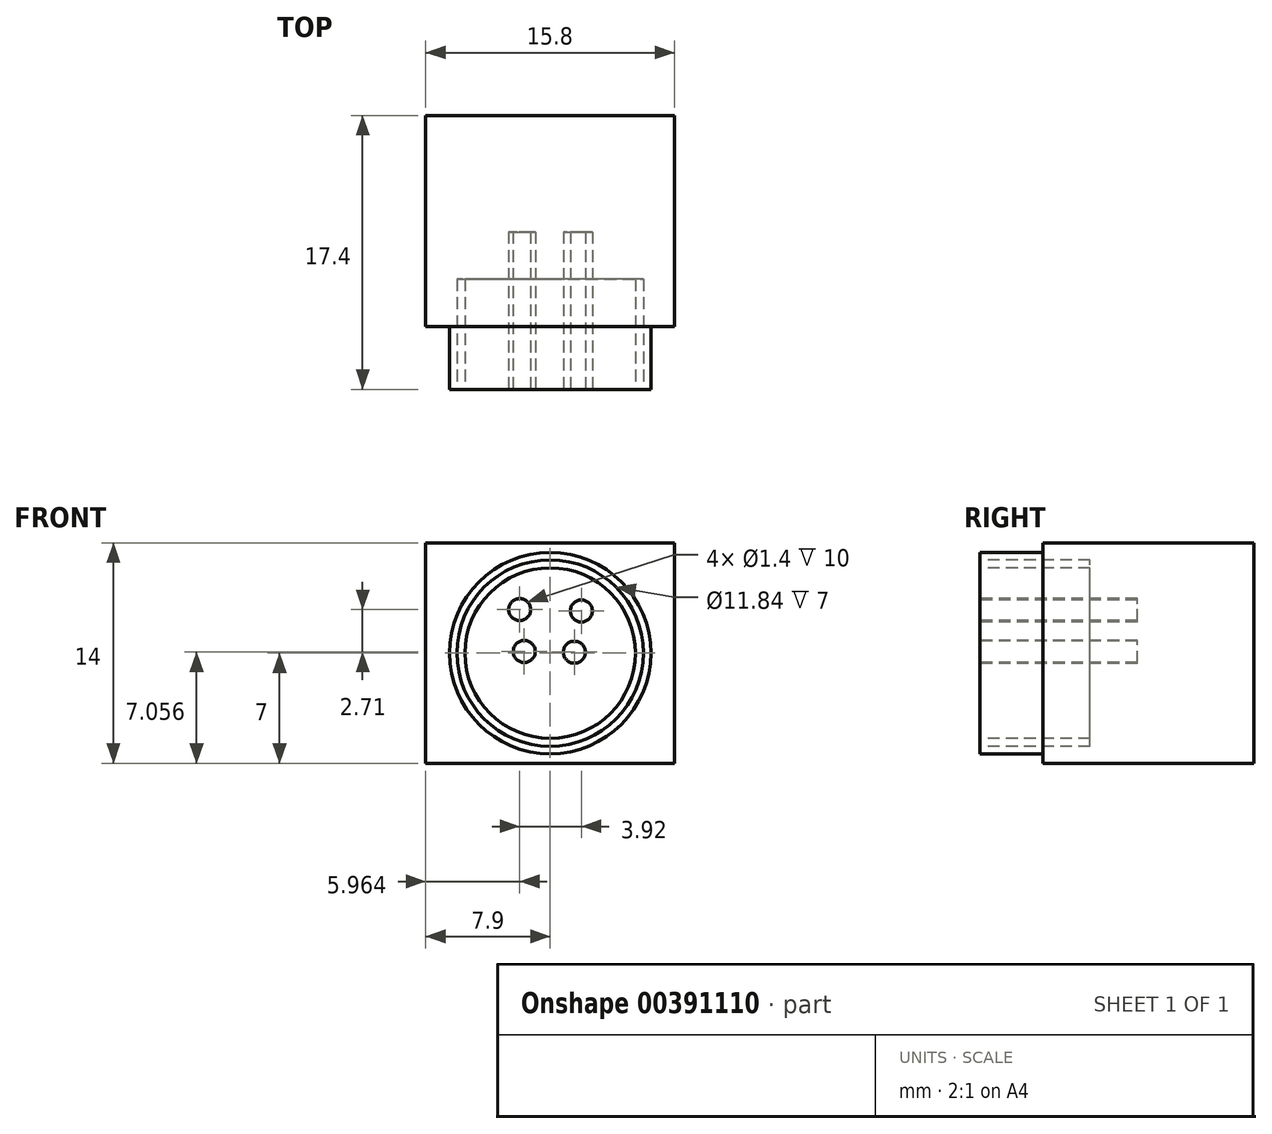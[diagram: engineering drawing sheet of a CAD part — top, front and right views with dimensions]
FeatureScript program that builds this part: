
annotation { "Feature Type Name" : "Feature", "Feature Type Description" : "" }
export const myFeature = defineFeature(function(context is Context, id is Id, definition is map)
    precondition{}
    {
        {
            var Q0;
            Q0=qCreatedBy(makeId("Front.planeOp"),FACE);
            var sketch = newSketch(context, id + "F0", { "sketchPlane" : qUnion([Q0])});
            skLineSegment(sketch, "E0.bottom", {"start": v(0, 0) * mm, "end": v(15.8, 0) * mm});
            skLineSegment(sketch, "E0.top", {"start": v(0, 14) * mm, "end": v(15.8, 14) * mm});
            skLineSegment(sketch, "E0.left", {"start": v(0, 0) * mm, "end": v(0, 14) * mm});
            skLineSegment(sketch, "E0.right", {"start": v(15.8, 0) * mm, "end": v(15.8, 14) * mm});
            skSolve(sketch);
        }
        {
            var Q0;
            Q0=qSketchRegion(id+"F0",true);
            extrude(context, id + "F1", {"entities" : qUnion([Q0]), "depth" : 13.4 * mm});
        }
        {
            var Q0;
            Q0=makeQuery(id+"F1.opExtrude","CAP_FACE",FACE,{"disambiguationData":[OSD([sQuery(id+"F0.wireOp",EDGE,"E0.bottom"),sQuery(id+"F0.wireOp",EDGE,"E0.top"),sQuery(id+"F0.wireOp",EDGE,"E0.left"),sQuery(id+"F0.wireOp",EDGE,"E0.right")])],"isStart":false});
            var sketch = newSketch(context, id + "F2", { "sketchPlane" : qUnion([Q0])});
            skCircle(sketch, "E1", {"center": v(7.9, 7) * mm, "radius": 6.4 * mm});
            skPoint(sketch, "E1.centerSnap0", {"position": v(15.8, 7) * mm});
            skPoint(sketch, "E1.centerSnap1", {"position": v(7.9, 14) * mm});
            skSolve(sketch);
        }
        {
            var Q0;
            Q0=qSketchRegion(id+"F2",true);
            extrude(context, id + "F3", {"entities" : qUnion([Q0]), "operationType" : NewBodyOperationType.ADD, "depth" : 4 * mm});
        }
        {
            var Q0;
            Q0=makeQuery(id+"F3.opExtrude","CAP_FACE",FACE,{"disambiguationData":[OSD([sQuery(id+"F2.wireOp",EDGE,"E1")])],"isStart":false});
            var sketch = newSketch(context, id + "F4", { "sketchPlane" : qUnion([Q0])});
            skCircle(sketch, "E2", {"center": v(7.9, 7) * mm, "radius": 5.92 * mm});
            skCircle(sketch, "E3", {"center": v(7.9, 7) * mm, "radius": 5.41 * mm});
            skSolve(sketch);
        }
        {
            var Q0;
            Q0=qSketchRegion(id+"F4",true);
            extrude(context, id + "F5", {"entities" : qUnion([Q0]), "operationType" : NewBodyOperationType.REMOVE, "oppositeDirection" : true, "depth" : 7 * mm});
        }
        {
            var Q0;
            Q0=makeQuery(id+"F5.boolean.opBoolean","SPLIT",FACE,{"disambiguationData":[TD([makeQuery(id+"F5.opExtrude","SWEPT_FACE",FACE,{"disambiguationData":[OSD([sQuery(id+"F4.wireOp",EDGE,"E3")])]})])],"derivedFrom":makeQuery(id+"F3.opExtrude","CAP_FACE",FACE,{"disambiguationData":[OSD([sQuery(id+"F2.wireOp",EDGE,"E1")])],"isStart":false})});
            var sketch = newSketch(context, id + "F6", { "sketchPlane" : qUnion([Q0])});
            skCircle(sketch, "E4", {"center": v(5.96, 9.77) * mm, "radius": 0.7 * mm});
            skCircle(sketch, "E5", {"center": v(9.88, 9.68) * mm, "radius": 0.7 * mm});
            skCircle(sketch, "E6", {"center": v(6.26, 7.1) * mm, "radius": 0.7 * mm});
            skCircle(sketch, "E7", {"center": v(9.44, 7.06) * mm, "radius": 0.7 * mm});
            skSolve(sketch);
        }
        {
            var Q0;
            Q0=qSketchRegion(id+"F6",true);
            extrude(context, id + "F7", {"entities" : qUnion([Q0]), "operationType" : NewBodyOperationType.REMOVE, "oppositeDirection" : true, "depth" : 10 * mm});
        }
    });
